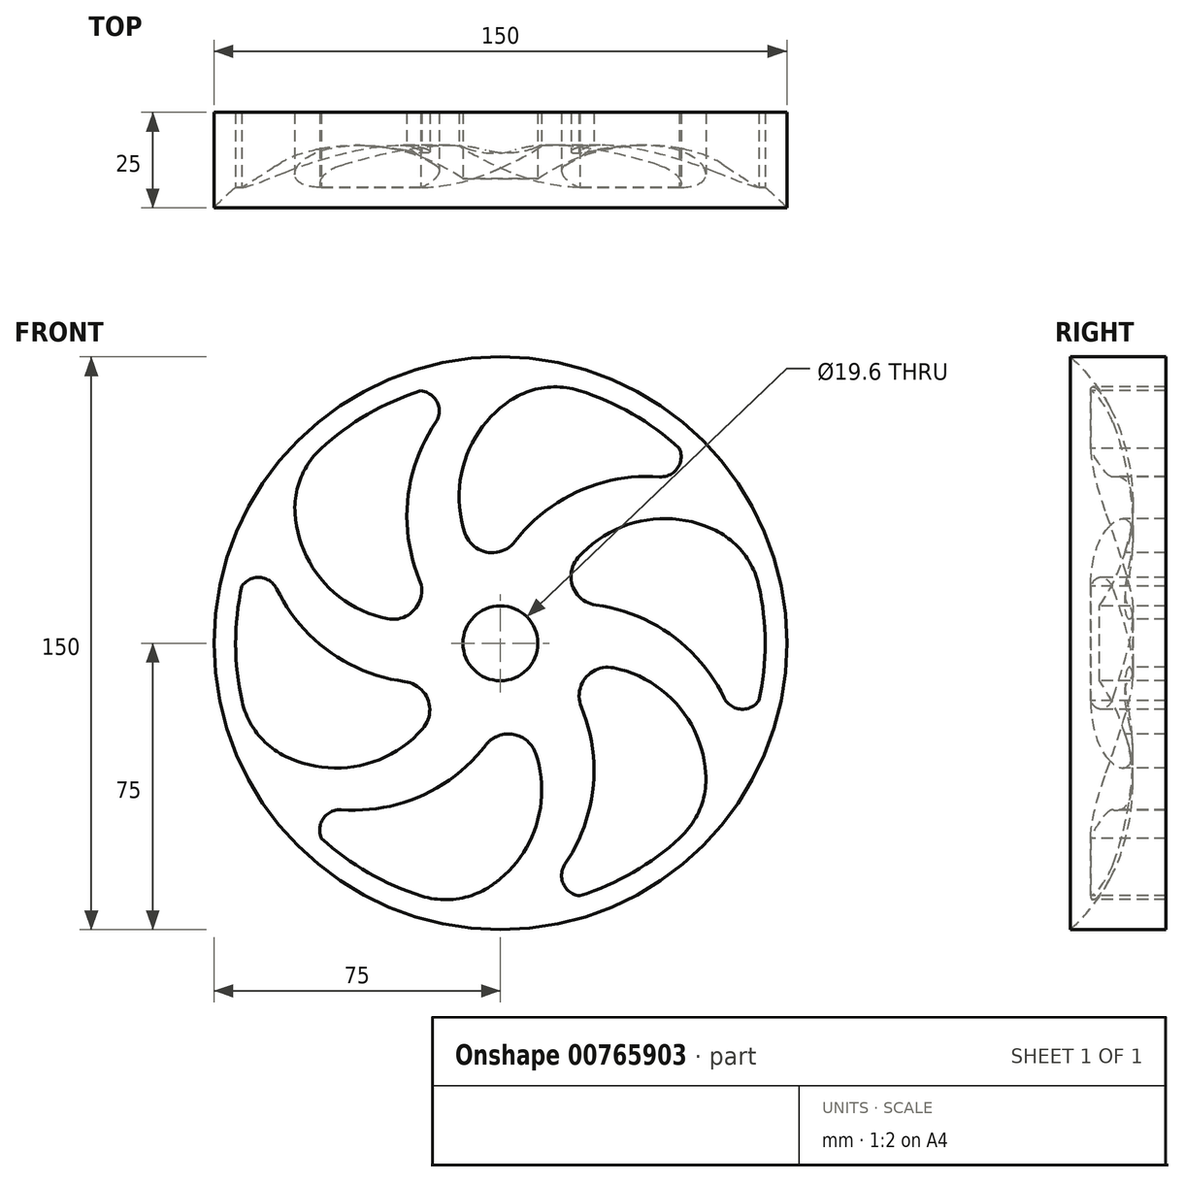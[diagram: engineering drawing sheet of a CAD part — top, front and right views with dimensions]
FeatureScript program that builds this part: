
annotation { "Feature Type Name" : "Feature", "Feature Type Description" : "" }
export const myFeature = defineFeature(function(context is Context, id is Id, definition is map)
    precondition{}
    {
        {
            var Q0;
            Q0=qCreatedBy(makeId("Front.planeOp"),FACE);
            var sketch = newSketch(context, id + "F0", { "sketchPlane" : qUnion([Q0])});
            skCircle(sketch, "E0", {"center": v(0, 0) * mm, "radius": 75 * mm});
            skCircle(sketch, "E1", {"center": v(0, 0) * mm, "radius": 72 * mm});
            skLineSegment(sketch, "E2", {"start": v(0, 0) * mm, "end": v(0, 81.37) * mm});
            skArc(sketch, "E3.trimOffspring", {"start": v(-16.93, 57.84) * mm, "mid": v(-24.25, 37.77) * mm, "end": v(-21.17, 16.63) * mm});
            skArc(sketch, "E4.trimOffspring", {"start": v(-53.75, 33.99) * mm, "mid": v(-46.33, 16.12) * mm, "end": v(-29.59, 6.42) * mm});
            skArc(sketch, "E5", {"start": v(-20.83, 66.1) * mm, "mid": v(-34.76, 59.95) * mm, "end": v(-47.01, 50.91) * mm});
            skArc(sketch, "E6.filletArc", {"start": v(-16.93, 57.84) * mm, "mid": v(-16.52, 63.08) * mm, "end": v(-20.83, 66.1) * mm});
            skArc(sketch, "E7.filletArc", {"start": v(-29.59, 6.42) * mm, "mid": v(-22.32, 9) * mm, "end": v(-21.17, 16.63) * mm});
            skArc(sketch, "E8.filletArc", {"start": v(-47.01, 50.91) * mm, "mid": v(-52.3, 43.22) * mm, "end": v(-53.75, 33.99) * mm});
            skArc(sketch, "E9.1.0", {"start": v(-58.56, 14.26) * mm, "mid": v(-44.83, -2.11) * mm, "end": v(-25, -10.02) * mm});
            skArc(sketch, "E9.1.1", {"start": v(-58.56, 14.26) * mm, "mid": v(-62.9, 17.23) * mm, "end": v(-67.65, 15.01) * mm});
            skArc(sketch, "E9.1.2", {"start": v(-67.65, 15.01) * mm, "mid": v(-69.3, -0.13) * mm, "end": v(-67.6, -15.26) * mm});
            skArc(sketch, "E9.1.3", {"start": v(-67.6, -15.26) * mm, "mid": v(-63.58, -23.69) * mm, "end": v(-56.3, -29.56) * mm});
            skArc(sketch, "E9.1.4", {"start": v(-56.3, -29.56) * mm, "mid": v(-37.12, -32.06) * mm, "end": v(-20.36, -22.41) * mm});
            skArc(sketch, "E9.1.5", {"start": v(-20.36, -22.41) * mm, "mid": v(-18.96, -14.83) * mm, "end": v(-25, -10.02) * mm});
            skLineSegment(sketch, "E9.1.6", {"start": v(0, 0) * mm, "end": v(-70.47, 40.69) * mm});
            skArc(sketch, "E9.2.0", {"start": v(-41.63, -43.58) * mm, "mid": v(-20.59, -39.88) * mm, "end": v(-3.82, -26.65) * mm});
            skArc(sketch, "E9.2.1", {"start": v(-41.63, -43.58) * mm, "mid": v(-46.37, -45.85) * mm, "end": v(-46.83, -51.08) * mm});
            skArc(sketch, "E9.2.2", {"start": v(-46.83, -51.08) * mm, "mid": v(-34.54, -60.08) * mm, "end": v(-20.59, -66.17) * mm});
            skArc(sketch, "E9.2.3", {"start": v(-20.59, -66.17) * mm, "mid": v(-11.27, -66.9) * mm, "end": v(-2.56, -63.54) * mm});
            skArc(sketch, "E9.2.4", {"start": v(-2.56, -63.54) * mm, "mid": v(9.2, -48.18) * mm, "end": v(9.23, -28.83) * mm});
            skArc(sketch, "E9.2.5", {"start": v(9.23, -28.83) * mm, "mid": v(3.36, -23.83) * mm, "end": v(-3.82, -26.65) * mm});
            skLineSegment(sketch, "E9.2.6", {"start": v(0, 0) * mm, "end": v(-70.47, -40.69) * mm});
            skArc(sketch, "E9.3.0", {"start": v(16.93, -57.84) * mm, "mid": v(24.25, -37.77) * mm, "end": v(21.17, -16.63) * mm});
            skArc(sketch, "E9.3.1", {"start": v(16.93, -57.84) * mm, "mid": v(16.52, -63.08) * mm, "end": v(20.83, -66.1) * mm});
            skArc(sketch, "E9.3.2", {"start": v(20.83, -66.1) * mm, "mid": v(34.76, -59.95) * mm, "end": v(47.01, -50.91) * mm});
            skArc(sketch, "E9.3.3", {"start": v(47.01, -50.91) * mm, "mid": v(52.3, -43.22) * mm, "end": v(53.75, -33.99) * mm});
            skArc(sketch, "E9.3.4", {"start": v(53.75, -33.99) * mm, "mid": v(46.33, -16.12) * mm, "end": v(29.59, -6.42) * mm});
            skArc(sketch, "E9.3.5", {"start": v(29.59, -6.42) * mm, "mid": v(22.32, -9) * mm, "end": v(21.17, -16.63) * mm});
            skLineSegment(sketch, "E9.3.6", {"start": v(0, 0) * mm, "end": v(0, -81.37) * mm});
            skArc(sketch, "E9.4.0", {"start": v(58.56, -14.26) * mm, "mid": v(44.83, 2.11) * mm, "end": v(25, 10.02) * mm});
            skArc(sketch, "E9.4.1", {"start": v(58.56, -14.26) * mm, "mid": v(62.9, -17.23) * mm, "end": v(67.65, -15.01) * mm});
            skArc(sketch, "E9.4.2", {"start": v(67.65, -15.01) * mm, "mid": v(69.3, 0.13) * mm, "end": v(67.6, 15.26) * mm});
            skArc(sketch, "E9.4.3", {"start": v(67.6, 15.26) * mm, "mid": v(63.58, 23.69) * mm, "end": v(56.3, 29.56) * mm});
            skArc(sketch, "E9.4.4", {"start": v(56.3, 29.56) * mm, "mid": v(37.12, 32.06) * mm, "end": v(20.36, 22.41) * mm});
            skArc(sketch, "E9.4.5", {"start": v(20.36, 22.41) * mm, "mid": v(18.96, 14.83) * mm, "end": v(25, 10.02) * mm});
            skLineSegment(sketch, "E9.4.6", {"start": v(0, 0) * mm, "end": v(70.47, -40.69) * mm});
            skArc(sketch, "E9.5.0", {"start": v(41.63, 43.58) * mm, "mid": v(20.59, 39.88) * mm, "end": v(3.82, 26.65) * mm});
            skArc(sketch, "E9.5.1", {"start": v(41.63, 43.58) * mm, "mid": v(46.37, 45.85) * mm, "end": v(46.83, 51.08) * mm});
            skArc(sketch, "E9.5.2", {"start": v(46.83, 51.08) * mm, "mid": v(34.54, 60.08) * mm, "end": v(20.59, 66.17) * mm});
            skArc(sketch, "E9.5.3", {"start": v(20.59, 66.17) * mm, "mid": v(11.27, 66.9) * mm, "end": v(2.56, 63.54) * mm});
            skArc(sketch, "E9.5.4", {"start": v(2.56, 63.54) * mm, "mid": v(-9.2, 48.18) * mm, "end": v(-9.23, 28.83) * mm});
            skArc(sketch, "E9.5.5", {"start": v(-9.23, 28.83) * mm, "mid": v(-3.36, 23.83) * mm, "end": v(3.82, 26.65) * mm});
            skLineSegment(sketch, "E9.5.6", {"start": v(0, 0) * mm, "end": v(70.47, 40.69) * mm});
            skCircle(sketch, "E10", {"center": v(0, 0) * mm, "radius": 13.2 * mm});
            skCircle(sketch, "E11", {"center": v(0, 0) * mm, "radius": 9.8 * mm});
            skSolve(sketch);
        }
        {
            var Q0;
            {var subQ6=sQuery(id+"F0.wireOp",EDGE,"E9.1.0");Q0=makeQuery(id+"F0.imprint","IMPRINT",FACE,{"disambiguationData":[TD([[makeQuery(id+"F0.imprint","IMPRINT",EDGE,{"derivedFrom":subQ6}),1.0]])]});}
            var Q1;
            {var subQ1=sQuery(id+"F0.wireOp",EDGE,"E3.trimOffspring");Q1=makeQuery(id+"F0.imprint","IMPRINT",FACE,{"disambiguationData":[TD([[makeQuery(id+"F0.imprint","IMPRINT",EDGE,{"derivedFrom":subQ1}),1.0]])]});}
            var Q2;
            {var subQ16=sQuery(id+"F0.wireOp",EDGE,"E9.5.0");Q2=makeQuery(id+"F0.imprint","IMPRINT",FACE,{"disambiguationData":[TD([[makeQuery(id+"F0.imprint","IMPRINT",EDGE,{"derivedFrom":subQ16}),1.0]])]});}
            var Q3;
            {var subQ8=sQuery(id+"F0.wireOp",EDGE,"E9.4.0");Q3=makeQuery(id+"F0.imprint","IMPRINT",FACE,{"disambiguationData":[TD([[makeQuery(id+"F0.imprint","IMPRINT",EDGE,{"derivedFrom":subQ8}),1.0]])]});}
            var Q4;
            {var subQ6=sQuery(id+"F0.wireOp",EDGE,"E9.3.0");Q4=makeQuery(id+"F0.imprint","IMPRINT",FACE,{"disambiguationData":[TD([[makeQuery(id+"F0.imprint","IMPRINT",EDGE,{"derivedFrom":subQ6}),1.0]])]});}
            var Q5;
            {var subQ6=sQuery(id+"F0.wireOp",EDGE,"E9.2.0");Q5=makeQuery(id+"F0.imprint","IMPRINT",FACE,{"disambiguationData":[TD([[makeQuery(id+"F0.imprint","IMPRINT",EDGE,{"derivedFrom":subQ6}),1.0]])]});}
            var Q6;
            {var subQ0=sQuery(id+"F0.wireOp",EDGE,"E2");var subQ1=sQuery(id+"F0.wireOp",EDGE,"E0");var subQ2=makeQuery(id+"F0.imprint","INTERSECT",VERTEX,{"derivedFrom":[subQ1,subQ0]});Q6=makeQuery(id+"F0.imprint","IMPRINT",FACE,{"disambiguationData":[TD([[makeQuery(id+"F0.imprint","IMPRINT",EDGE,{"disambiguationData":[TD([[subQ2,1.0]])],"derivedFrom":subQ1}),1.0]])]});}
            var Q7;
            {var subQ0=sQuery(id+"F0.wireOp",EDGE,"E2");var subQ1=sQuery(id+"F0.wireOp",EDGE,"E0");var subQ2=makeQuery(id+"F0.imprint","INTERSECT",VERTEX,{"derivedFrom":[subQ1,subQ0]});Q7=makeQuery(id+"F0.imprint","IMPRINT",FACE,{"disambiguationData":[TD([[makeQuery(id+"F0.imprint","IMPRINT",EDGE,{"disambiguationData":[TD([[subQ2,-1.0]])],"derivedFrom":subQ1}),1.0]])]});}
            var Q8;
            {var subQ0=sQuery(id+"F0.wireOp",EDGE,"E9.1.6");var subQ1=sQuery(id+"F0.wireOp",EDGE,"E0");var subQ2=makeQuery(id+"F0.imprint","INTERSECT",VERTEX,{"derivedFrom":[subQ1,subQ0]});Q8=makeQuery(id+"F0.imprint","IMPRINT",FACE,{"disambiguationData":[TD([[makeQuery(id+"F0.imprint","IMPRINT",EDGE,{"disambiguationData":[TD([[subQ2,-1.0]])],"derivedFrom":subQ1}),1.0]])]});}
            var Q9;
            {var subQ0=sQuery(id+"F0.wireOp",EDGE,"E9.2.6");var subQ1=sQuery(id+"F0.wireOp",EDGE,"E0");var subQ2=makeQuery(id+"F0.imprint","INTERSECT",VERTEX,{"derivedFrom":[subQ1,subQ0]});Q9=makeQuery(id+"F0.imprint","IMPRINT",FACE,{"disambiguationData":[TD([[makeQuery(id+"F0.imprint","IMPRINT",EDGE,{"disambiguationData":[TD([[subQ2,-1.0]])],"derivedFrom":subQ1}),1.0]])]});}
            var Q10;
            {var subQ0=sQuery(id+"F0.wireOp",EDGE,"E9.3.6");var subQ1=sQuery(id+"F0.wireOp",EDGE,"E0");var subQ2=makeQuery(id+"F0.imprint","INTERSECT",VERTEX,{"derivedFrom":[subQ1,subQ0]});Q10=makeQuery(id+"F0.imprint","IMPRINT",FACE,{"disambiguationData":[TD([[makeQuery(id+"F0.imprint","IMPRINT",EDGE,{"disambiguationData":[TD([[subQ2,-1.0]])],"derivedFrom":subQ1}),1.0]])]});}
            var Q11;
            {var subQ0=sQuery(id+"F0.wireOp",EDGE,"E9.5.6");var subQ1=sQuery(id+"F0.wireOp",EDGE,"E0");var subQ2=makeQuery(id+"F0.imprint","INTERSECT",VERTEX,{"derivedFrom":[subQ1,subQ0]});Q11=makeQuery(id+"F0.imprint","IMPRINT",FACE,{"disambiguationData":[TD([[makeQuery(id+"F0.imprint","IMPRINT",EDGE,{"disambiguationData":[TD([[subQ2,1.0]])],"derivedFrom":subQ1}),1.0]])]});}
            var Q12;
            {var subQ0=sQuery(id+"F0.wireOp",EDGE,"E11");var subQ1=sQuery(id+"F0.wireOp",EDGE,"E2");var subQ2=makeQuery(id+"F0.imprint","INTERSECT",VERTEX,{"derivedFrom":[subQ1,subQ0]});Q12=makeQuery(id+"F0.imprint","IMPRINT",FACE,{"disambiguationData":[TD([[makeQuery(id+"F0.imprint","IMPRINT",EDGE,{"disambiguationData":[TD([[subQ2,-1.0]])],"derivedFrom":subQ1}),-1.0]])]});}
            var Q13;
            {var subQ0=sQuery(id+"F0.wireOp",EDGE,"E11");var subQ1=sQuery(id+"F0.wireOp",EDGE,"E9.4.6");var subQ2=makeQuery(id+"F0.imprint","INTERSECT",VERTEX,{"derivedFrom":[subQ1,subQ0]});Q13=makeQuery(id+"F0.imprint","IMPRINT",FACE,{"disambiguationData":[TD([[makeQuery(id+"F0.imprint","IMPRINT",EDGE,{"disambiguationData":[TD([[subQ2,-1.0]])],"derivedFrom":subQ1}),1.0]])]});}
            var Q14;
            {var subQ0=sQuery(id+"F0.wireOp",EDGE,"E11");var subQ1=sQuery(id+"F0.wireOp",EDGE,"E9.3.6");var subQ2=makeQuery(id+"F0.imprint","INTERSECT",VERTEX,{"derivedFrom":[subQ1,subQ0]});Q14=makeQuery(id+"F0.imprint","IMPRINT",FACE,{"disambiguationData":[TD([[makeQuery(id+"F0.imprint","IMPRINT",EDGE,{"disambiguationData":[TD([[subQ2,-1.0]])],"derivedFrom":subQ1}),1.0]])]});}
            var Q15;
            {var subQ0=sQuery(id+"F0.wireOp",EDGE,"E11");var subQ1=sQuery(id+"F0.wireOp",EDGE,"E9.2.6");var subQ2=makeQuery(id+"F0.imprint","INTERSECT",VERTEX,{"derivedFrom":[subQ1,subQ0]});Q15=makeQuery(id+"F0.imprint","IMPRINT",FACE,{"disambiguationData":[TD([[makeQuery(id+"F0.imprint","IMPRINT",EDGE,{"disambiguationData":[TD([[subQ2,-1.0]])],"derivedFrom":subQ1}),1.0]])]});}
            var Q16;
            {var subQ0=sQuery(id+"F0.wireOp",EDGE,"E11");var subQ1=sQuery(id+"F0.wireOp",EDGE,"E9.1.6");var subQ2=makeQuery(id+"F0.imprint","INTERSECT",VERTEX,{"derivedFrom":[subQ1,subQ0]});Q16=makeQuery(id+"F0.imprint","IMPRINT",FACE,{"disambiguationData":[TD([[makeQuery(id+"F0.imprint","IMPRINT",EDGE,{"disambiguationData":[TD([[subQ2,-1.0]])],"derivedFrom":subQ1}),1.0]])]});}
            var Q17;
            {var subQ0=sQuery(id+"F0.wireOp",EDGE,"E11");var subQ1=sQuery(id+"F0.wireOp",EDGE,"E2");var subQ2=makeQuery(id+"F0.imprint","INTERSECT",VERTEX,{"derivedFrom":[subQ1,subQ0]});Q17=makeQuery(id+"F0.imprint","IMPRINT",FACE,{"disambiguationData":[TD([[makeQuery(id+"F0.imprint","IMPRINT",EDGE,{"disambiguationData":[TD([[subQ2,-1.0]])],"derivedFrom":subQ1}),1.0]])]});}
            extrude(context, id + "F1", {"entities" : qUnion([Q0, Q1, Q2, Q3, Q4, Q5, Q6, Q7, Q8, Q9, Q10, Q11, Q12, Q13, Q14, Q15, Q16, Q17]), "oppositeDirection" : true, "depth" : 25 * mm, "offsetDistance" : 25 * mm});
        }
        {
            var Q0;
            Q0=qCreatedBy(makeId("Top.planeOp"),FACE);
            var sketch = newSketch(context, id + "F2", { "sketchPlane" : qUnion([Q0])});
            skLineSegment(sketch, "E12", {"start": v(0, 0) * mm, "end": v(0, 45) * mm});
            skLineSegment(sketch, "E13", {"start": v(0, 0) * mm, "end": v(-1, 0) * mm});
            skLineSegment(sketch, "E14", {"start": v(-1, 0) * mm, "end": v(-75, 0) * mm});
            skArc(sketch, "E15", {"start": v(-1, 0) * mm, "mid": v(-38, 16.37) * mm, "end": v(-75, 0) * mm});
            skSolve(sketch);
        }
        {
            var Q0;
            Q0=makeQuery(id+"F2.imprint","IMPRINT",FACE,{"disambiguationData":[TD([[makeQuery(id+"F2.imprint","IMPRINT",EDGE,{"derivedFrom":sQuery(id+"F2.wireOp",EDGE,"E14")}),-1.0]])]});
            var Q1;
            Q1=sQuery(id+"F2.wireOp",EDGE,"E12");
            revolve(context, id + "F3", {"operationType" : NewBodyOperationType.REMOVE, "surfaceOperationType" : NewSurfaceOperationType.NEW, "entities" : qUnion([Q0]), "axis" : qUnion([Q1]), "revolveType" : RevolveType.ONE_DIRECTION, "oppositeDirection" : true, "angle" : 360 * degree});
        }
    });
